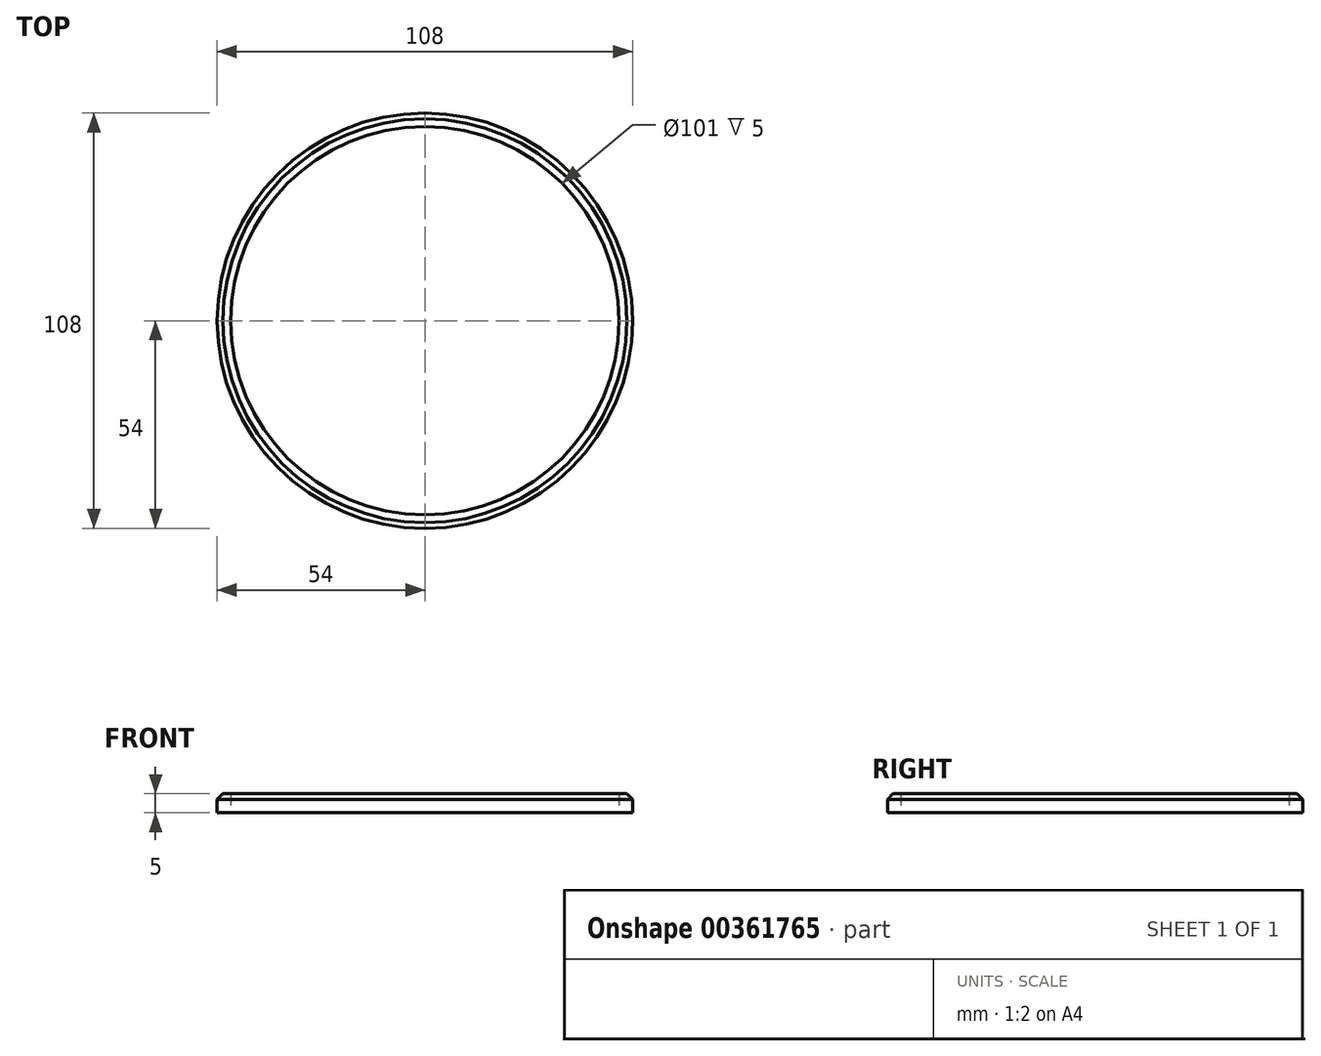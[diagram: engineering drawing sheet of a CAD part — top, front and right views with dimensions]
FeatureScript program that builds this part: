
annotation { "Feature Type Name" : "Feature", "Feature Type Description" : "" }
export const myFeature = defineFeature(function(context is Context, id is Id, definition is map)
    precondition{}
    {
        {
            var Q0;
            Q0=qCreatedBy(makeId("Top.planeOp"),FACE);
            var sketch = newSketch(context, id + "F0", { "sketchPlane" : qUnion([Q0])});
            skCircle(sketch, "E0", {"center": v(0, -2.53) * mm, "radius": 50.5 * mm});
            skCircle(sketch, "E1.0", {"center": v(0, -2.53) * mm, "radius": 54 * mm});
            skSolve(sketch);
        }
        {
            var Q0;
            Q0=makeQuery(id+"F0.imprint","IMPRINT",FACE,{"disambiguationData":[TD([[makeQuery(id+"F0.imprint","IMPRINT",EDGE,{"derivedFrom":sQuery(id+"F0.wireOp",EDGE,"E0")}),-1.0]])]});
            extrude(context, id + "F1", {"entities" : qUnion([Q0]), "depth" : 5 * mm, "offsetDistance" : 25 * mm});
        }
        {
            var Q0;
            Q0=makeQuery(id+"F1.opExtrude","CAP_EDGE",EDGE,{"disambiguationData":[OSD([sQuery(id+"F0.wireOp",EDGE,"E1.0")])],"isStart":false});
            chamfer(context, id + "F2", {"entities" : qUnion([Q0]), "width" : 1.5 * mm, "tangentPropagation" : true});
        }
    });
